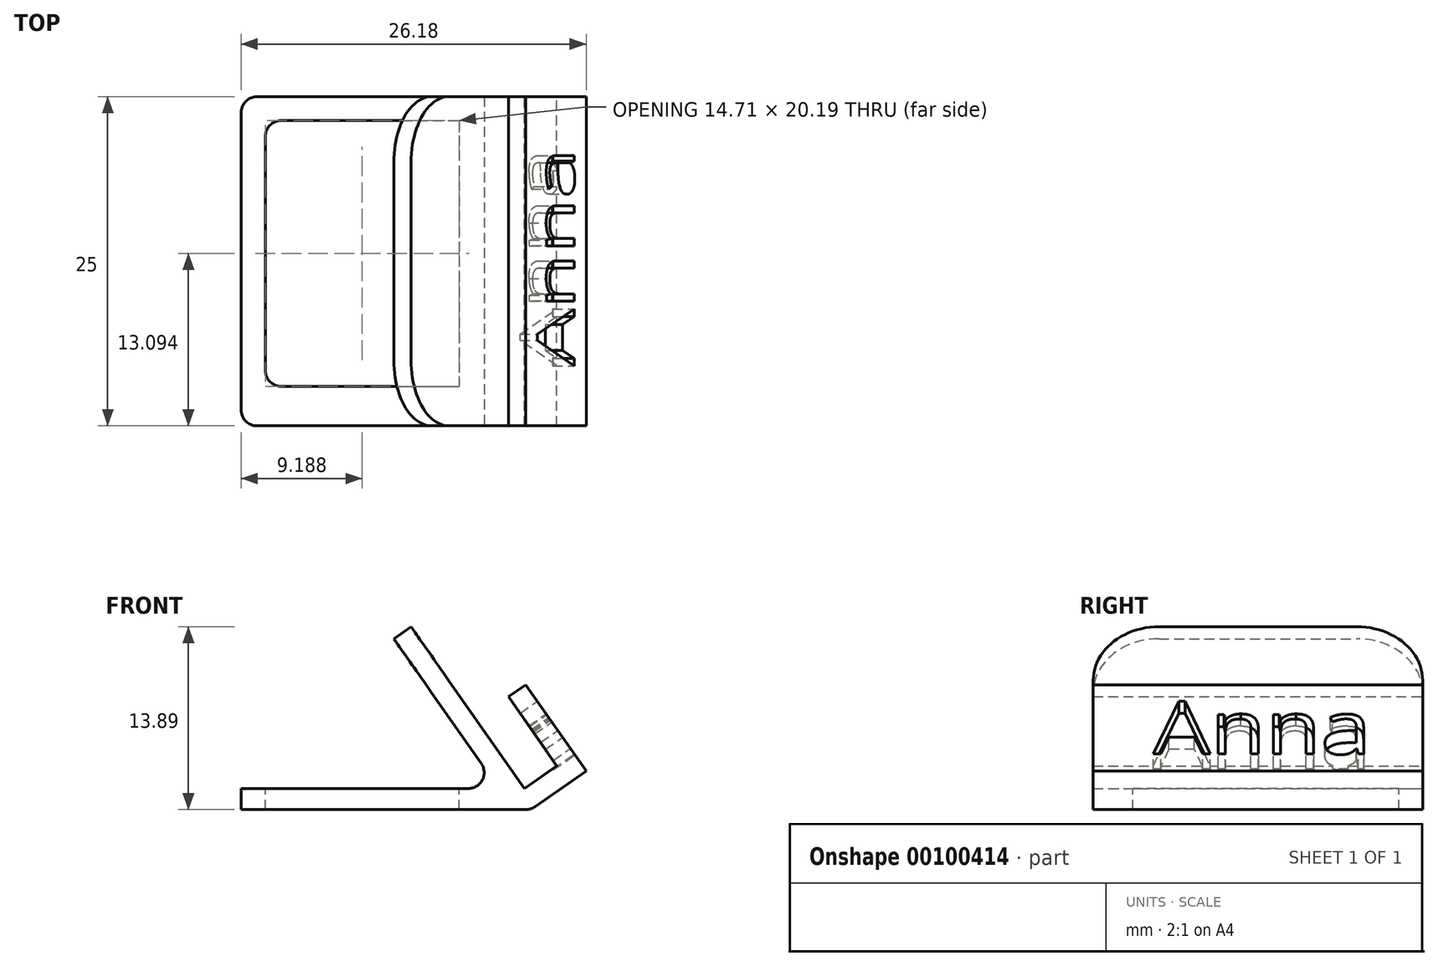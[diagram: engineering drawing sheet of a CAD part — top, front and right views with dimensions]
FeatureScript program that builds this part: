
annotation { "Feature Type Name" : "Feature", "Feature Type Description" : "" }
export const myFeature = defineFeature(function(context is Context, id is Id, definition is map)
    precondition{}
    {
        {
            var Q0;
            Q0=qCreatedBy(makeId("Front.planeOp"),FACE);
            var sketch = newSketch(context, id + "F0", { "sketchPlane" : qUnion([Q0])});
            skLineSegment(sketch, "E0", {"start": v(0, 0) * mm, "end": v(22, 0) * mm});
            skLineSegment(sketch, "E1", {"start": v(22, 0) * mm, "end": v(26.18, 2.93) * mm});
            skLineSegment(sketch, "E2", {"start": v(26.18, 2.93) * mm, "end": v(21.6, 9.48) * mm});
            skLineSegment(sketch, "E3", {"start": v(21.6, 9.48) * mm, "end": v(20.28, 8.56) * mm});
            skLineSegment(sketch, "E4", {"start": v(20.28, 8.56) * mm, "end": v(23.95, 3.32) * mm});
            skLineSegment(sketch, "E5", {"start": v(23.95, 3.32) * mm, "end": v(21.5, 1.6) * mm});
            skLineSegment(sketch, "E6", {"start": v(21.5, 1.6) * mm, "end": v(12.9, 13.89) * mm});
            skLineSegment(sketch, "E7", {"start": v(12.9, 13.89) * mm, "end": v(11.58, 12.97) * mm});
            skLineSegment(sketch, "E8", {"start": v(11.58, 12.97) * mm, "end": v(19.54, 1.6) * mm});
            skLineSegment(sketch, "E9", {"start": v(19.54, 1.6) * mm, "end": v(0, 1.6) * mm});
            skLineSegment(sketch, "E10", {"start": v(0, 1.6) * mm, "end": v(0, 0) * mm});
            skLineSegment(sketch, "E11", {"start": v(23.95, 3.32) * mm, "end": v(24.87, 2.01) * mm, "construction": true});
            skSolve(sketch);
        }
        {
            var Q0;
            Q0 = qSketchRegion(id + "F0", true);
            extrude(context, id + "F1", {"entities" : qUnion([Q0]), "depth" : 25 * mm});
        }
        {
            var Q0;
            Q0=makeQuery(id+"F1.opExtrude","CAP_FACE",FACE,{"disambiguationData":[OSD([sQuery(id+"F0.wireOp",EDGE,"E0"),sQuery(id+"F0.wireOp",EDGE,"E1"),sQuery(id+"F0.wireOp",EDGE,"E2"),sQuery(id+"F0.wireOp",EDGE,"E3"),sQuery(id+"F0.wireOp",EDGE,"E4"),sQuery(id+"F0.wireOp",EDGE,"E5"),sQuery(id+"F0.wireOp",EDGE,"E6"),sQuery(id+"F0.wireOp",EDGE,"E7"),sQuery(id+"F0.wireOp",EDGE,"E8"),sQuery(id+"F0.wireOp",EDGE,"E9"),sQuery(id+"F0.wireOp",EDGE,"E10")])],"isStart":true});
            cPlane(context, id + "F2", {"entities" : qUnion([Q0]), "cplaneType" : CPlaneType.OFFSET, "offset" : 5 * mm, "oppositeDirection" : true, "width" : 150 * mm, "height" : 150 * mm});
        }
        {
            var Q0;
            Q0=qCreatedBy(id+"F2.planeOp",FACE);
            var sketch = newSketch(context, id + "F3", { "sketchPlane" : qUnion([Q0])});
            skLineSegment(sketch, "E12.0", {"start": v(-21.5, 1.6) * mm, "end": v(-12.9, 13.89) * mm});
            skLineSegment(sketch, "E13.0", {"start": v(-11.58, 12.97) * mm, "end": v(-19.54, 1.6) * mm});
            skLineSegment(sketch, "E14.0", {"start": v(-12.9, 13.89) * mm, "end": v(-11.58, 12.97) * mm});
            skLineSegment(sketch, "E15", {"start": v(-21.5, 1.6) * mm, "end": v(-19.54, 1.6) * mm});
            skSolve(sketch);
        }
        {
            var Q0;
            Q0=makeQuery(id+"FEYjz0NULyM1hZZ_1.boolean.opBoolean","MERGE",FACE,{"derivedFrom":[makeQuery(id+"F1.opExtrude","SWEPT_FACE",FACE,{"disambiguationData":[OSD([sQuery(id+"F0.wireOp",EDGE,"E9")])]}),makeQuery(id+"FEYjz0NULyM1hZZ_1.opExtrude","SWEPT_FACE",FACE,{"disambiguationData":[OSD([sQuery(id+"F3.wireOp",EDGE,"E15")])]})]});
            var sketch = newSketch(context, id + "F4", { "sketchPlane" : qUnion([Q0])});
            skLineSegment(sketch, "E16.bottom", {"start": v(1.83, -1.81) * mm, "end": v(16.54, -1.81) * mm});
            skLineSegment(sketch, "E16.top", {"start": v(1.83, -22) * mm, "end": v(16.54, -22) * mm});
            skLineSegment(sketch, "E16.left", {"start": v(1.83, -1.81) * mm, "end": v(1.83, -22) * mm});
            skLineSegment(sketch, "E16.right", {"start": v(16.54, -1.81) * mm, "end": v(16.54, -22) * mm});
            skSolve(sketch);
        }
        {
            var Q0;
            Q0 = qSketchRegion(id + "F4", true);
            extrude(context, id + "F5", {"entities" : qUnion([Q0]), "operationType" : NewBodyOperationType.REMOVE, "oppositeDirection" : true, "depth" : 25 * mm});
        }
        {
            var Q0;
            {var subQ0=sQuery(id+"F3.wireOp",EDGE,"E15");var subQ1=sQuery(id+"F0.wireOp",EDGE,"E9");var subQ2=sQuery(id+"F0.wireOp",EDGE,"E8");Q0=makeQuery(id+"FEYjz0NULyM1hZZ_1.boolean.opBoolean","SPLIT",EDGE,{"disambiguationData":[TD([makeQuery(id+"FEYjz0NULyM1hZZ_1.opExtrude","CAP_FACE",FACE,{"disambiguationData":[OSD([sQuery(id+"F3.wireOp",EDGE,"E12.0"),sQuery(id+"F3.wireOp",EDGE,"E13.0"),sQuery(id+"F3.wireOp",EDGE,"E14.0"),subQ0])],"isStart":true})])],"derivedFrom":makeQuery(id+"F1.opExtrude","SWEPT_EDGE",EDGE,{"disambiguationData":[OSD([subQ2,subQ1])]})});}
            var Q1;
            {var subQ0=sQuery(id+"F3.wireOp",EDGE,"E15");var subQ1=sQuery(id+"F0.wireOp",EDGE,"E8");var subQ2=sQuery(id+"F0.wireOp",EDGE,"E9");Q1=makeQuery(id+"FEYjz0NULyM1hZZ_1.boolean.opBoolean","SPLIT",EDGE,{"disambiguationData":[TD([makeQuery(id+"FEYjz0NULyM1hZZ_1.opExtrude","CAP_FACE",FACE,{"disambiguationData":[OSD([sQuery(id+"F3.wireOp",EDGE,"E12.0"),sQuery(id+"F3.wireOp",EDGE,"E13.0"),sQuery(id+"F3.wireOp",EDGE,"E14.0"),subQ0])],"isStart":false})])],"derivedFrom":makeQuery(id+"F1.opExtrude","SWEPT_EDGE",EDGE,{"disambiguationData":[OSD([subQ1,subQ2])]})});}
            var Q2;
            Q2=makeQuery(id+"F1.opExtrude","SWEPT_EDGE",EDGE,{"disambiguationData":[OSD([sQuery(id+"F0.wireOp",EDGE,"E0"),sQuery(id+"F0.wireOp",EDGE,"E1")])]});
            var Q3;
            Q3=makeQuery(id+"F1.opExtrude","CAP_EDGE",EDGE,{"disambiguationData":[OSD([sQuery(id+"F0.wireOp",EDGE,"E10")])],"isStart":false});
            var Q4;
            Q4=makeQuery(id+"F5.boolean.opBoolean","COPY",EDGE,{"derivedFrom":makeQuery(id+"F5.opExtrude","SWEPT_EDGE",EDGE,{"disambiguationData":[OSD([sQuery(id+"F4.wireOp",EDGE,"E16.top"),sQuery(id+"F4.wireOp",EDGE,"E16.left")])]})});
            var Q5;
            Q5=makeQuery(id+"F5.boolean.opBoolean","COPY",EDGE,{"derivedFrom":makeQuery(id+"F5.opExtrude","SWEPT_EDGE",EDGE,{"disambiguationData":[OSD([sQuery(id+"F4.wireOp",EDGE,"E16.bottom"),sQuery(id+"F4.wireOp",EDGE,"E16.left")])]})});
            var Q6;
            Q6=makeQuery(id+"F1.opExtrude","CAP_EDGE",EDGE,{"disambiguationData":[OSD([sQuery(id+"F0.wireOp",EDGE,"E10")])],"isStart":true});
            fillet(context, id + "F6", {"entities" : qUnion([Q0, Q1, Q2, Q3, Q4, Q5, Q6]), "radius" : 1.2 * mm, "tangentPropagation" : true, "allowEdgeOverflow" : false});
        }
        {
            var Q0;
            Q0=makeQuery(id+"F1.opExtrude","CAP_EDGE",EDGE,{"disambiguationData":[OSD([sQuery(id+"F0.wireOp",EDGE,"E7")])],"isStart":false});
            var Q1;
            Q1=makeQuery(id+"F1.opExtrude","CAP_EDGE",EDGE,{"disambiguationData":[OSD([sQuery(id+"F0.wireOp",EDGE,"E7")])],"isStart":true});
            fillet(context, id + "F7", {"entities" : qUnion([Q0, Q1]), "radius" : 5 * mm, "tangentPropagation" : true, "allowEdgeOverflow" : false});
        }
        {
            var Q0;
            Q0=makeQuery(id+"F1.opExtrude","SWEPT_FACE",FACE,{"disambiguationData":[OSD([sQuery(id+"F0.wireOp",EDGE,"E2")])]});
            var sketch = newSketch(context, id + "F8", { "sketchPlane" : qUnion([Q0])});
            skText(sketch, "E17", { "text": "Anna", "fontName": "OpenSans-Regular.ttf"});
            const initialGuessF8  = {"E17": [-0.02044, -0.01105, 1, 0, 0.00492]};
            skSetInitialGuess(sketch, initialGuessF8);
            skSolve(sketch);
        }
        {
            var Q0;
            Q0 = qSketchRegion(id + "F8", true);
            extrude(context, id + "F9", {"entities" : qUnion([Q0]), "operationType" : NewBodyOperationType.REMOVE, "oppositeDirection" : true, "depth" : 2 * mm});
        }
        {
            var Q0;
            Q0=makeQuery(id+"F9.boolean.opBoolean","SPLIT",FACE,{"disambiguationData":[TD([makeQuery(id+"F9.opExtrude","SWEPT_FACE",FACE,{"disambiguationData":[OSD([sQuery(id+"F8.wireOp",EDGE,"E17.sketch_text.stroke-66")])]})])],"derivedFrom":makeQuery(id+"F1.opExtrude","SWEPT_FACE",FACE,{"disambiguationData":[OSD([sQuery(id+"F0.wireOp",EDGE,"E2")])]})});
            extrude(context, id + "F10", {"entities" : qUnion([Q0]), "operationType" : NewBodyOperationType.REMOVE, "oppositeDirection" : true, "depth" : 2 * mm});
        }
        {
            var Q0;
            Q0=makeQuery(id+"F9.boolean.opBoolean","SPLIT",FACE,{"disambiguationData":[TD([makeQuery(id+"F9.opExtrude","SWEPT_FACE",FACE,{"disambiguationData":[OSD([sQuery(id+"F8.wireOp",EDGE,"E17.sketch_text.stroke-8")])]})])],"derivedFrom":makeQuery(id+"F1.opExtrude","SWEPT_FACE",FACE,{"disambiguationData":[OSD([sQuery(id+"F0.wireOp",EDGE,"E2")])]})});
            extrude(context, id + "F11", {"entities" : qUnion([Q0]), "operationType" : NewBodyOperationType.REMOVE, "oppositeDirection" : true, "depth" : 2 * mm});
        }
    });
